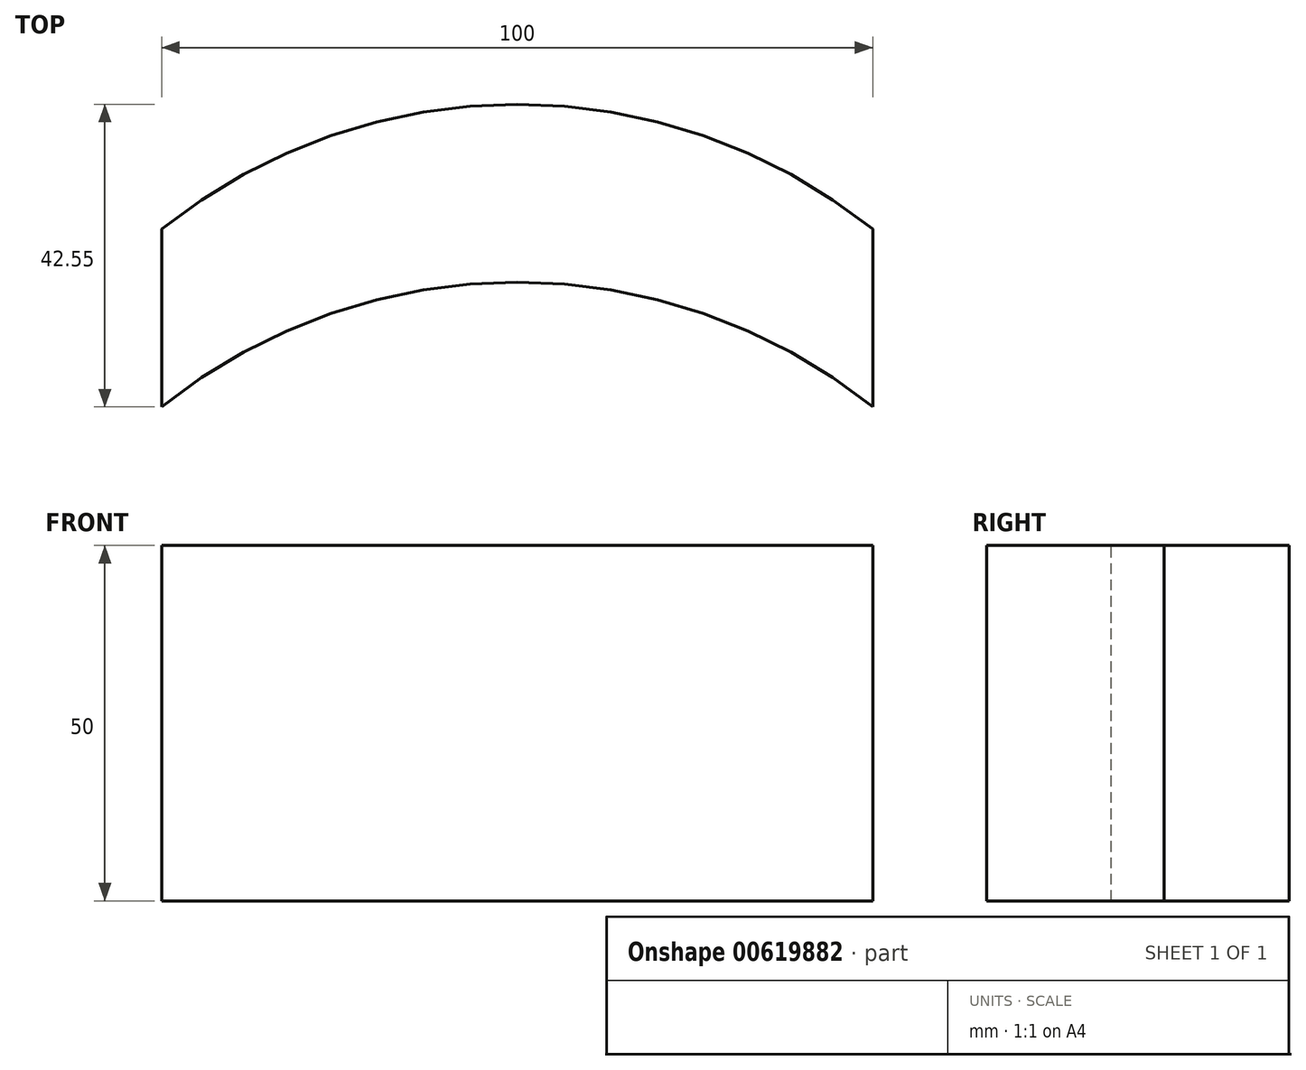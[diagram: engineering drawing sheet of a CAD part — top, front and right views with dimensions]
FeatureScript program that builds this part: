
annotation { "Feature Type Name" : "Feature", "Feature Type Description" : "" }
export const myFeature = defineFeature(function(context is Context, id is Id, definition is map)
    precondition{}
    {
        {
            var Q0;
            Q0=qCreatedBy(makeId("Top.planeOp"),FACE);
            var sketch = newSketch(context, id + "F0", { "sketchPlane" : qUnion([Q0])});
            skArc(sketch, "E0", {"start": v(50, 0) * mm, "mid": v(0, 17.55) * mm, "end": v(-50, 0) * mm});
            skLineSegment(sketch, "E1", {"start": v(-50, 0) * mm, "end": v(-50, 25) * mm});
            skLineSegment(sketch, "E2", {"start": v(50, 0) * mm, "end": v(50, 25) * mm});
            skArc(sketch, "E3", {"start": v(50, 25) * mm, "mid": v(0, 42.55) * mm, "end": v(-50, 25) * mm});
            skSolve(sketch);
        }
        {
            var Q0;
            Q0=makeQuery(id+"F0.imprint","IMPRINT",FACE,{"disambiguationData":[TD([[makeQuery(id+"F0.imprint","IMPRINT",EDGE,{"derivedFrom":sQuery(id+"F0.wireOp",EDGE,"E0")}),-1.0]])]});
            extrude(context, id + "F1", {"entities" : qUnion([Q0]), "oppositeDirection" : true, "depth" : 50 * mm});
        }
    });
